# Revit family: Seating-Lounge-Bernhard_Design-Mitt
name_source: partatom
category: Furniture
revit_build: Autodesk Revit Architecture 2013 (Build: 20130531_2115(x64)
units: mm (PartAtom-declared; Revit-internal decimal feet)

## types (4) — shared parameters
Depth = 2' - 9 1/2"
Description = Lounge
Height = 2' - 8"
Manufacturer = Bernhardt Design
Product Documentation Link = http://www.bernhardtdesign.com
Product Name = Mitt
Product Page URL = http://www.bernhardtdesign.com
Seat Height = 1' - 4 1/2"
URL = http://bernhardtdesign.com
Width = 2' - 9 1/2"

## per-type parameters (varying)
| type | Handle | Upholstery |
| 5720 | Yes | Fabric- Bernhardt Design - Blue Linen |
| 5720L | Yes | Leather - Bernhardt Design - Brown |
| 5721 | No | Fabric- Bernhardt Design - Blue Linen |
| 5721L | No | Leather - Bernhardt Design - Brown |

note: column(s) folded — value = type name in every type: Model

## geometry (parser evidence)
native form markers: Blend x50, Sweep x1
no freeform markers — native parametric forms only
